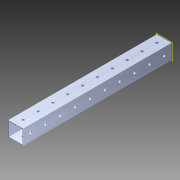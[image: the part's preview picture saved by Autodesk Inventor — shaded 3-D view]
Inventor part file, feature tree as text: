
AUTODESK INVENTOR PART (.ipt)
format: ipt  version: 2014 SP1 (Build 180222100, 222)  size: 1,164,800 bytes
history: native  units: in
note: dims shown in document units (in); Inventor stores cm internally (conversion verified against a paired STEP export)
features: pattern_circular x1, other x1, plane x1, extrude x1, imported_body x1, sketch x1
ambient origin geometry x8: Origin, YZ Plane, XZ Plane, XY Plane, X Axis, Y Axis, Z Axis, Center Point
bodies: Body1 (feature_tree)
feature tree (6):
  pattern_circular  "CirPattern2"
  other  "217-3426-STEP1"
  plane  "Work Plane1"
  extrude  "Extrusion1"  Depth=3937.0079in TaperAngle=0.0deg
  imported_body  "Base1"
  sketch  "Sketch1"  dims[d0=-10.0in d1=3937.0079in d2=0.0in]
